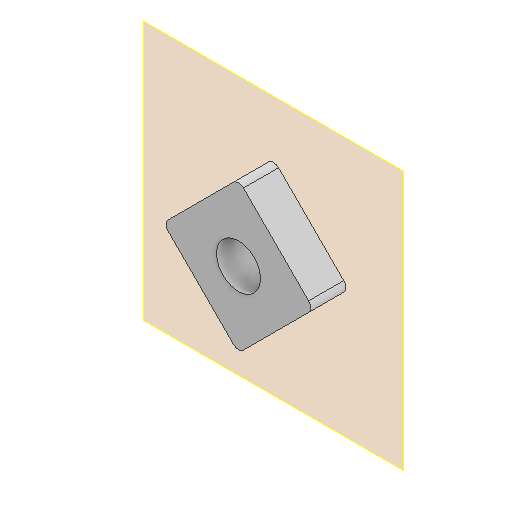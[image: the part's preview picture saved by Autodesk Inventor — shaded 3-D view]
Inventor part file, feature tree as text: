
AUTODESK INVENTOR PART (.ipt)
format: ipt  version: 2022 (Build 260153000, 153)  size: 113,664 bytes
history: native  units: mm
features: other x2, plane x1, extrude x1, sketch x1, reference x1
ambient origin geometry x8: Origin, YZ Plane, XZ Plane, XY Plane, X Axis, Y Axis, Z Axis, Center Point
bodies: Volumenkörper1 (feature_tree)
feature tree (6):
  plane  "Arbeitsebene1"
  extrude  "Extrusion1"  Depth=10.0mm
  sketch  "Skizze1"  dims[d0=0.5mm d1=10.0mm d2=8.0mm d3=0.0mm]
  reference  "Referenz1"
  other  "Assembly_Matchboxscope_injectionmolded.iam"
  other  "IM_Matchboxscope_plate:2"
